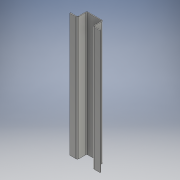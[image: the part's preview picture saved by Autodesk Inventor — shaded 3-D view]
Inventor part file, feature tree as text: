
AUTODESK INVENTOR PART (.ipt)
format: ipt  version: 2017 (Build 210142000, 142)  size: 161,280 bytes
history: native  units: mm
features: sheet_metal_op x3, other x2, sketch x1
ambient origin geometry x8: Origin, YZ Plane, XZ Plane, XY Plane, X Axis, Y Axis, Z Axis, Center Point
bodies: Solid1 (feature_tree)
feature tree (6):
  sheet_metal_op  "Contour Flange1"
  sketch  "Sketch1"  dims[d0=30.0mm d1=15.0mm d3=18.5mm d4=15.0mm d5=15.0mm d6=1.5mm d7=0.75mm d8=3.0mm d9=1.5mm d10=245.0mm d11=1.5mm d12=0.5mm d13=6.0mm d14=1.5mm d15=1.5mm]
  other  "Plate1"
  sheet_metal_op  "Bend1"
  sheet_metal_op  "Corner1"
  other  "Definition1"
